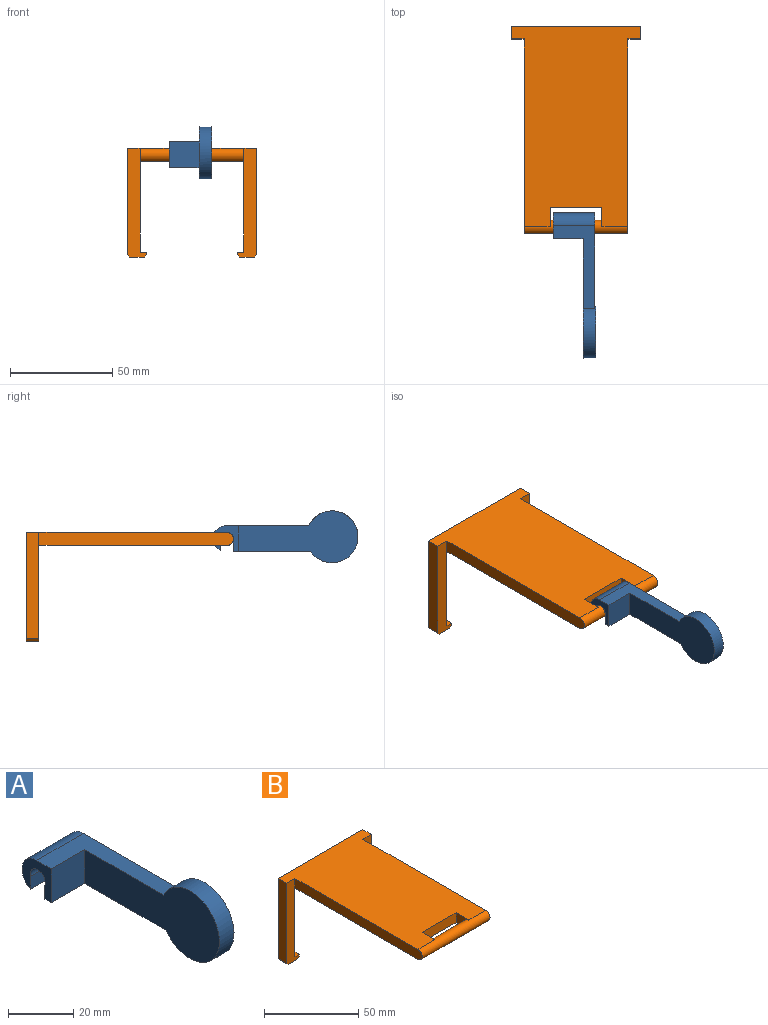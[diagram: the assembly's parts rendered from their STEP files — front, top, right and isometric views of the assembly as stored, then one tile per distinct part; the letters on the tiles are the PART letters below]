
ASSEMBLY  parts=2 mates=1
PART A: 12 faces, bbox 20.9x71.1x25.4 mm
  f0: plane 12.7x12.7mm, normal (-1,0,0), area 89.1mm2, adj f1,f2,f4,f5,f6,f7,f11
  f1: plane 38.04x20.32mm, normal (0,0,-1), area 260.6mm2, adj f0,f3,f5,f8,f9,f11
  f2: plane 40.58x20.32mm, normal (0,0,1), area 328mm2, adj f0,f3,f4,f8,f9,f11
  f3: plane 48.01x12.7mm, normal (1,0,0), area 516mm2, adj f1,f2,f4,f5,f6,f7,f8
  f4: cylinder r=6.35mm len=20.32mm, axis (-1,0,0), area 350.9mm2, adj f0,f2,f3,f7
  f5: plane 20.32x5.26mm, normal (0,1,0), area 106.9mm2, adj f0,f1,f3,f6
  f6: cylinder r=3.24mm len=20.32mm, axis (-1,0,0), area 243.6mm2, adj f0,f3,f5,f7
  f7: plane 20.32x4.84mm, normal (0,-1,0), area 98.3mm2, adj f0,f3,f4,f6
  f8: cylinder r=12.7mm len=25.4mm, axis (1,0,0), area 429.1mm2, adj f1,f2,f3,f9,f10
  f9: plane 58.42x25.4mm, normal (-1,0,0), area 933.6mm2, adj f1,f2,f8,f11
  f10: plane 25.4x25.4mm, normal (1,0,0), area 506.7mm2, adj f8
  f11: plane 14.51x12.7mm, normal (0,-1,0), area 184.3mm2, adj f0,f1,f2,f9
PART B: 25 faces, bbox 63.5x101.6x53.2 mm
  f0: plane 44.45x6.35mm, normal (-1,0,0), area 282.3mm2, adj f4,f5,f6,f15
  f1: plane 95.25x6.35mm, normal (-1,0,0), area 600.5mm2, adj f3,f4,f10,f21
  f2: plane 95.25x6.35mm, normal (1,0,0), area 600.5mm2, adj f3,f4,f6,f21
  f3: plane 98.43x63.5mm, normal (0,0,1), area 4838.7mm2, adj f1,f2,f5,f6,f7,f9,f10,f21
  f4: plane 98.43x50.8mm, normal (0,0,-1), area 4758.1mm2, adj f0,f1,f2,f5,f8,f21,f22,f23
  f5: plane 63.5x53.24mm, normal (0,1,0), area 1011.5mm2, adj f0,f3,f4,f7,f8,f9,f11,f12
  f6: plane 53.24x9.53mm, normal (0,-1,0), area 344.5mm2, adj f0,f2,f3,f7,f11,f15,f16,f17
  f7: plane 52.07x6.35mm, normal (1,0,0), area 330.6mm2, adj f3,f5,f6,f11
  f8: plane 44.45x6.35mm, normal (1,0,0), area 282.3mm2, adj f4,f5,f10,f13
  f9: plane 52.07x6.35mm, normal (-1,0,0), area 330.6mm2, adj f3,f5,f10,f12
  f10: plane 53.24x9.53mm, normal (0,-1,0), area 344.4mm2, adj f1,f3,f8,f9,f12,f13,f14,f18
  f11: plane 6.35x1.17mm, normal (0.71,0,-0.71), area 10.5mm2, adj f5,f6,f7,f19
  f12: plane 6.35x1.17mm, normal (-0.71,0,-0.71), area 10.5mm2, adj f5,f9,f10,f20
  f13: plane 6.35x3.18mm, normal (0,0,1), area 20.2mm2, adj f5,f8,f10,f14
  f14: plane 6.35x1.27mm, normal (1,0,0), area 8.1mm2, adj f5,f10,f13,f18
  f15: plane 6.35x3.18mm, normal (0,0,1), area 20.2mm2, adj f0,f5,f6,f16
  f16: plane 6.35x1.27mm, normal (-1,0,0), area 8.1mm2, adj f5,f6,f15,f17
  f17: plane 6.35x1.17mm, normal (-0.71,0,-0.71), area 10.5mm2, adj f5,f6,f16,f19
  f18: plane 6.35x1.17mm, normal (0.71,0,-0.71), area 10.5mm2, adj f5,f10,f14,f20
  f19: plane 7.18x6.35mm, normal (0,0,-1), area 45.6mm2, adj f5,f6,f11,f17
  f20: plane 7.18x6.35mm, normal (0,0,-1), area 45.6mm2, adj f5,f10,f12,f18
  f21: cylinder r=3.17mm len=50.8mm, axis (1,0,0), area 760.1mm2, adj f1,f2,f3,f4,f23,f24
  f22: plane 25.4x6.35mm, normal (0,-1,0), area 161.3mm2, adj f3,f4,f23,f24
  f23: plane 9.53x6.35mm, normal (-1,0,0), area 44.6mm2, adj f3,f4,f21,f22
  f24: plane 9.53x6.35mm, normal (1,0,0), area 44.6mm2, adj f3,f4,f21,f22
PLACE A t=(136.22,-71.77,-23.19)mm
PLACE B t=(120.08,19.78,-8.95)mm
MATE cylindrical B.f21 <-> A.f6  axis (1,0,0) through (126.43,-78.65,-5.77)mm
